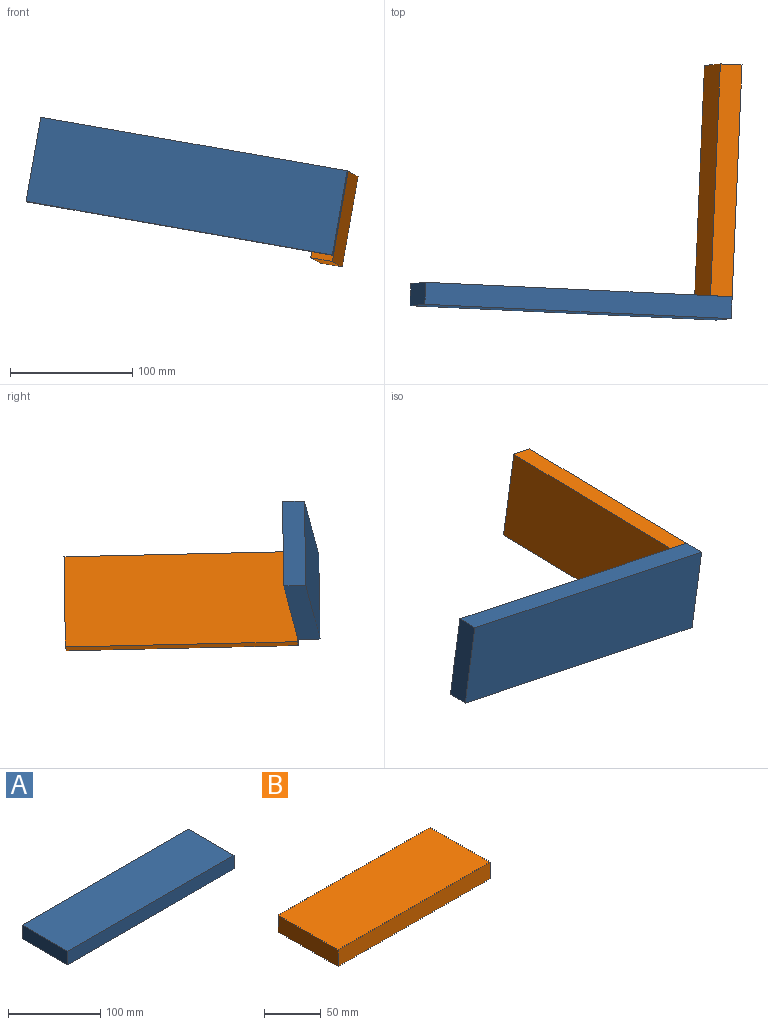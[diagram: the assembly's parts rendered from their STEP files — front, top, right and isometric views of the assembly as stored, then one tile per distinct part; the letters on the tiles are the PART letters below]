
ASSEMBLY  parts=2 mates=1
PART A: 6 faces, bbox 255x70x18 mm
  f0: plane 70x18mm, normal (-1,0,0), area 1260mm2, adj f1,f3,f4,f5
  f1: plane 255x18mm, normal (0,-1,0), area 4590mm2, adj f0,f2,f4,f5
  f2: plane 70x18mm, normal (1,0,0), area 1260mm2, adj f1,f3,f4,f5
  f3: plane 255x18mm, normal (0,1,0), area 4590mm2, adj f0,f2,f4,f5
  f4: plane 255x70mm, normal (0,0,1), area 17850mm2, adj f0,f1,f2,f3
  f5: plane 255x70mm, normal (0,0,-1), area 17850mm2, adj f0,f1,f2,f3
PART B: 6 faces, bbox 190x75x18 mm
  f0: plane 75x18mm, normal (-1,0,0), area 1350mm2, adj f1,f3,f4,f5
  f1: plane 190x18mm, normal (0,-1,0), area 3420mm2, adj f0,f2,f4,f5
  f2: plane 75x18mm, normal (1,0,0), area 1350mm2, adj f1,f3,f4,f5
  f3: plane 190x18mm, normal (0,1,0), area 3420mm2, adj f0,f2,f4,f5
  f4: plane 190x75mm, normal (0,0,1), area 14250mm2, adj f0,f1,f2,f3
  f5: plane 190x75mm, normal (0,0,-1), area 14250mm2, adj f0,f1,f2,f3
PLACE A rot(axis=(-0.99,0.11,0.06),91.5deg) t=(-23.51,-133.99,82.89)mm
PLACE B rot(axis=(0.62,0.61,0.5),123.9deg) t=(197.49,-128,-32.18)mm
MATE fastened B.f3 <-> A.f1  axis (0.17,0.02,0.98) through (228.17,-127.69,38.58)mm
